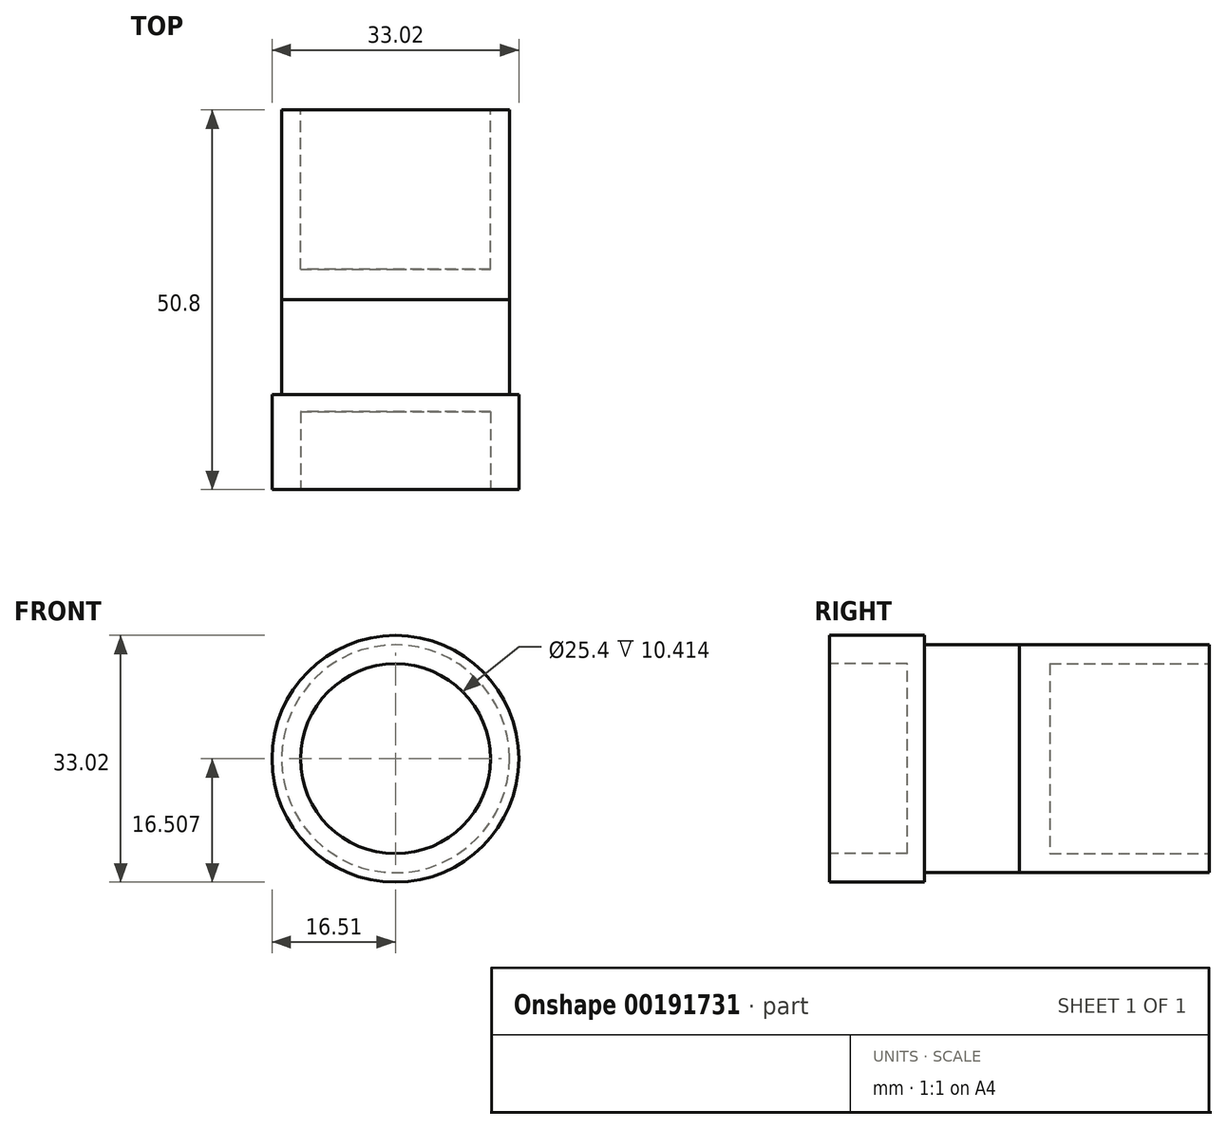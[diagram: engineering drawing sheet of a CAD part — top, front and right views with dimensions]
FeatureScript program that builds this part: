
annotation { "Feature Type Name" : "Feature", "Feature Type Description" : "" }
export const myFeature = defineFeature(function(context is Context, id is Id, definition is map)
    precondition{}
    {
        {
            var Q0;
            Q0=qCreatedBy(makeId("Front.planeOp"),FACE);
            var sketch = newSketch(context, id + "F0", { "sketchPlane" : qUnion([Q0])});
            skCircle(sketch, "E0", {"center": v(0, 7.87) * mm, "radius": 16.51 * mm});
            skSolve(sketch);
        }
        {
            var Q0;
            Q0 = qSketchRegion(id + "F0", true);
            extrude(context, id + "F1", {"entities" : qUnion([Q0]), "depth" : 12.7 * mm});
        }
        {
            var Q0;
            Q0=makeQuery(id+"F1.opExtrude","CAP_FACE",FACE,{"disambiguationData":[OSD([sQuery(id+"F0.wireOp",EDGE,"E0")])],"isStart":true});
            var sketch = newSketch(context, id + "F2", { "sketchPlane" : qUnion([Q0])});
            skCircle(sketch, "E1", {"center": v(0, 7.87) * mm, "radius": 15.24 * mm});
            skSolve(sketch);
        }
        {
            var Q0;
            Q0 = qSketchRegion(id + "F2", true);
            extrude(context, id + "F3", {"entities" : qUnion([Q0]), "operationType" : NewBodyOperationType.ADD, "depth" : 12.7 * mm});
        }
        {
            var Q0;
            Q0=makeQuery(id+"F1.opExtrude","CAP_FACE",FACE,{"disambiguationData":[OSD([sQuery(id+"F0.wireOp",EDGE,"E0")])],"isStart":false});
            var sketch = newSketch(context, id + "F4", { "sketchPlane" : qUnion([Q0])});
            skCircle(sketch, "E2", {"center": v(0, 7.87) * mm, "radius": 12.7 * mm});
            skSolve(sketch);
        }
        {
            var Q0;
            Q0=makeQuery(id+"F4.imprint","IMPRINT",FACE,{"disambiguationData":[TD([[makeQuery(id+"F4.imprint","IMPRINT",EDGE,{"derivedFrom":sQuery(id+"F4.wireOp",EDGE,"E2")}),1.0]])]});
            extrude(context, id + "F5", {"entities" : qUnion([Q0]), "operationType" : NewBodyOperationType.REMOVE, "oppositeDirection" : true, "depth" : 10.4 * mm});
        }
        {
            var Q0;
            Q0=makeQuery(id+"F3.opExtrude","CAP_FACE",FACE,{"disambiguationData":[OSD([sQuery(id+"F2.wireOp",EDGE,"E1")])],"isStart":false});
            var sketch = newSketch(context, id + "F6", { "sketchPlane" : qUnion([Q0])});
            skCircle(sketch, "E3", {"center": v(0, 7.87) * mm, "radius": 12.7 * mm});
            skSolve(sketch);
        }
        {
            var Q0;
            Q0=makeQuery(id+"F6.imprint","IMPRINT",FACE,{"disambiguationData":[TD([[makeQuery(id+"F6.imprint","IMPRINT",EDGE,{"derivedFrom":sQuery(id+"F6.wireOp",EDGE,"E3")}),1.0]])]});
            var Q1;
            Q1=makeQuery(id+"F6.imprint","IMPRINT",FACE,{"disambiguationData":[TD([[makeQuery(id+"F6.imprint","IMPRINT",EDGE,{"derivedFrom":sQuery(id+"F6.wireOp",EDGE,"E3")}),-1.0]])]});
            var Q2;
            Q2=makeQuery(id+"F3.opExtrude","CAP_FACE",FACE,{"disambiguationData":[OSD([sQuery(id+"F2.wireOp",EDGE,"E1")])],"isStart":false});
            extrude(context, id + "F7", {"entities" : qUnion([Q0, Q1, Q2]), "depth" : 25.4 * mm});
        }
        {
            var Q0;
            {var subQ0=sQuery(id+"F2.wireOp",EDGE,"E1");Q0=makeQuery(id+"F7.opExtrude","CAP_FACE",FACE,{"disambiguationData":[OSD([subQ0]),TDD([makeQuery(id+"F3.opExtrude","CAP_FACE",FACE,{"disambiguationData":[OSD([subQ0])],"isStart":false})])],"isStart":false});}
            var sketch = newSketch(context, id + "F8", { "sketchPlane" : qUnion([Q0])});
            skCircle(sketch, "E4", {"center": v(0, 7.87) * mm, "radius": 12.7 * mm});
            skSolve(sketch);
        }
        {
            var Q0;
            Q0=makeQuery(id+"F8.imprint","IMPRINT",FACE,{"disambiguationData":[TD([[makeQuery(id+"F8.imprint","IMPRINT",EDGE,{"derivedFrom":sQuery(id+"F8.wireOp",EDGE,"E4")}),1.0]])]});
            extrude(context, id + "F9", {"entities" : qUnion([Q0]), "oppositeDirection" : true, "depth" : 21.34 * mm});
        }
    });
